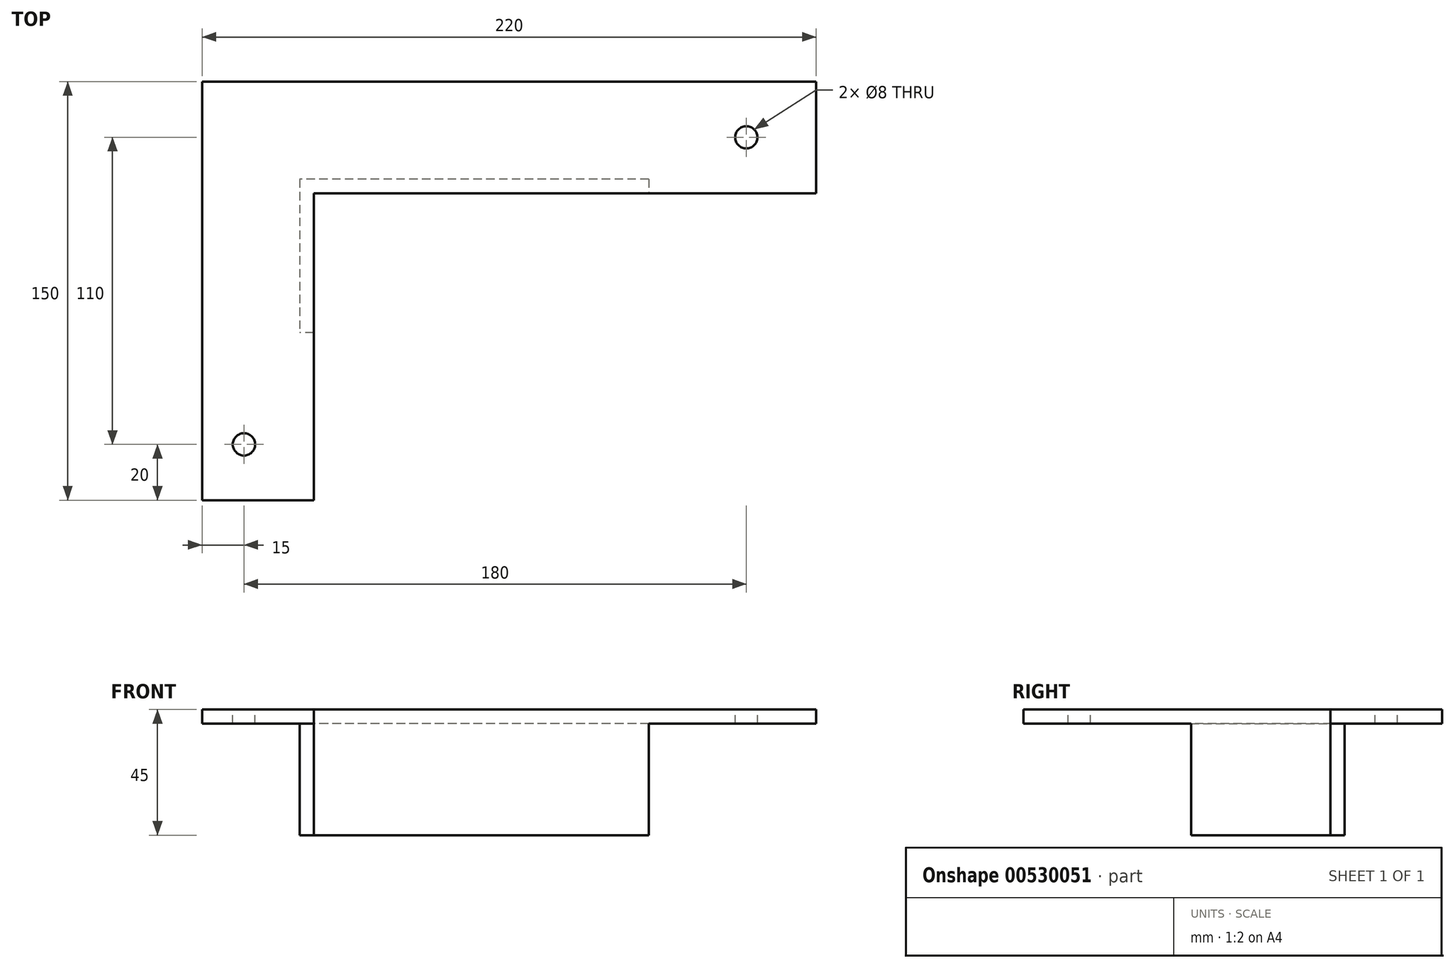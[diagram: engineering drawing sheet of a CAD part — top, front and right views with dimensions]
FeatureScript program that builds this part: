
annotation { "Feature Type Name" : "Feature", "Feature Type Description" : "" }
export const myFeature = defineFeature(function(context is Context, id is Id, definition is map)
    precondition{}
    {
        {
            var Q0;
            Q0=qCreatedBy(makeId("Top.planeOp"),FACE);
            var sketch = newSketch(context, id + "F0", { "sketchPlane" : qUnion([Q0])});
            skLineSegment(sketch, "E0.bottom", {"start": v(110, -20) * mm, "end": v(-110, -20) * mm});
            skLineSegment(sketch, "E0.top", {"start": v(110, 20) * mm, "end": v(-110, 20) * mm});
            skLineSegment(sketch, "E0.left", {"start": v(110, -20) * mm, "end": v(110, 20) * mm});
            skLineSegment(sketch, "E0.right", {"start": v(-110, -20) * mm, "end": v(-110, 20) * mm});
            skPoint(sketch, "E0.middle", {"position": v(0, 0) * mm});
            skSolve(sketch);
        }
        {
            var Q0;
            Q0=makeQuery(id+"F0.imprint","IMPRINT",FACE,{"disambiguationData":[TD([[makeQuery(id+"F0.imprint","IMPRINT",EDGE,{"derivedFrom":sQuery(id+"F0.wireOp",EDGE,"E0.bottom")}),-1.0]])]});
            extrude(context, id + "F1", {"entities" : qUnion([Q0]), "depth" : 5 * mm, "offsetDistance" : 25 * mm});
        }
        {
            var Q0;
            Q0=makeQuery(id+"F1.opExtrude","CAP_FACE",FACE,{"disambiguationData":[OSD([sQuery(id+"F0.wireOp",EDGE,"E0.bottom"),sQuery(id+"F0.wireOp",EDGE,"E0.top"),sQuery(id+"F0.wireOp",EDGE,"E0.left"),sQuery(id+"F0.wireOp",EDGE,"E0.right")])],"isStart":true});
            var sketch = newSketch(context, id + "F2", { "sketchPlane" : qUnion([Q0])});
            skLineSegment(sketch, "E1", {"start": v(110, 20) * mm, "end": v(50, 20) * mm});
            skLineSegment(sketch, "E2", {"start": v(50, 15) * mm, "end": v(50, 20) * mm});
            skLineSegment(sketch, "E3", {"start": v(50, 15) * mm, "end": v(-70, 15) * mm});
            skLineSegment(sketch, "E4", {"start": v(-70, 15) * mm, "end": v(-70, 20) * mm});
            skSolve(sketch);
        }
        {
            var Q0;
            Q0=qSketchRegion(id+"F2",true);
            var Q1;
            {var subQ0=sQuery(id+"F2.wireOp",EDGE,"E2");Q1=makeQuery(id+"F2.imprint","IMPRINT",FACE,{"disambiguationData":[TD([[makeQuery(id+"F2.imprint","IMPRINT",EDGE,{"derivedFrom":subQ0}),1.0]])]});}
            extrude(context, id + "F3", {"entities" : qUnion([Q0, Q1]), "operationType" : NewBodyOperationType.ADD, "depth" : 40 * mm, "offsetDistance" : 25 * mm});
        }
        {
            var Q0;
            Q0=makeQuery(id+"F1.opExtrude","CAP_FACE",FACE,{"disambiguationData":[OSD([sQuery(id+"F0.wireOp",EDGE,"E0.bottom"),sQuery(id+"F0.wireOp",EDGE,"E0.top"),sQuery(id+"F0.wireOp",EDGE,"E0.left"),sQuery(id+"F0.wireOp",EDGE,"E0.right")])],"isStart":true});
            var sketch = newSketch(context, id + "F4", { "sketchPlane" : qUnion([Q0])});
            skLineSegment(sketch, "E5", {"start": v(-110, 20) * mm, "end": v(-110, 130) * mm});
            skLineSegment(sketch, "E6", {"start": v(-110, 130) * mm, "end": v(-70, 130) * mm});
            skLineSegment(sketch, "E7", {"start": v(-70, 130) * mm, "end": v(-70, 20) * mm});
            skSolve(sketch);
        }
        {
            var Q0;
            Q0=qSketchRegion(id+"F4",true);
            var Q1;
            Q1=makeQuery(id+"F4.imprint","IMPRINT",FACE,{"disambiguationData":[TD([[makeQuery(id+"F4.imprint","IMPRINT",EDGE,{"derivedFrom":sQuery(id+"F4.wireOp",EDGE,"E5")}),-1.0]])]});
            extrude(context, id + "F5", {"entities" : qUnion([Q0, Q1]), "operationType" : NewBodyOperationType.ADD, "oppositeDirection" : true, "depth" : 5 * mm, "offsetDistance" : 25 * mm});
        }
        {
            var Q0;
            {var subQ0=sQuery(id+"F0.wireOp",EDGE,"E0.bottom");Q0=makeQuery(id+"F5.boolean.opBoolean","MERGE",FACE,{"derivedFrom":[makeQuery(id+"F1.opExtrude","CAP_FACE",FACE,{"disambiguationData":[OSD([subQ0,sQuery(id+"F0.wireOp",EDGE,"E0.top"),sQuery(id+"F0.wireOp",EDGE,"E0.left"),sQuery(id+"F0.wireOp",EDGE,"E0.right")])],"isStart":true}),makeQuery(id+"F5.opExtrude","CAP_FACE",FACE,{"disambiguationData":[OSD([subQ0,sQuery(id+"F4.wireOp",EDGE,"E5"),sQuery(id+"F4.wireOp",EDGE,"E6"),sQuery(id+"F4.wireOp",EDGE,"E7")])],"isStart":true})]});}
            var sketch = newSketch(context, id + "F6", { "sketchPlane" : qUnion([Q0])});
            skLineSegment(sketch, "E8", {"start": v(-70, 15) * mm, "end": v(-75, 15) * mm});
            skLineSegment(sketch, "E9", {"start": v(-70, 15) * mm, "end": v(-70, 70) * mm});
            skLineSegment(sketch, "E10", {"start": v(-70, 70) * mm, "end": v(-75, 70) * mm});
            skLineSegment(sketch, "E11", {"start": v(-75, 15) * mm, "end": v(-75, 70) * mm});
            skSolve(sketch);
        }
        {
            var Q0;
            Q0=qSketchRegion(id+"F6",true);
            var Q1;
            Q1=makeQuery(id+"F6.imprint","IMPRINT",FACE,{"disambiguationData":[TD([[makeQuery(id+"F6.imprint","IMPRINT",EDGE,{"derivedFrom":sQuery(id+"F6.wireOp",EDGE,"E8")}),-1.0]])]});
            extrude(context, id + "F7", {"entities" : qUnion([Q0, Q1]), "operationType" : NewBodyOperationType.ADD, "depth" : 40 * mm, "offsetDistance" : 25 * mm});
        }
        {
            var Q0;
            {var subQ0=sQuery(id+"F0.wireOp",EDGE,"E0.bottom");Q0=makeQuery(id+"F5.boolean.opBoolean","MERGE",FACE,{"derivedFrom":[makeQuery(id+"F1.opExtrude","CAP_FACE",FACE,{"disambiguationData":[OSD([subQ0,sQuery(id+"F0.wireOp",EDGE,"E0.top"),sQuery(id+"F0.wireOp",EDGE,"E0.left"),sQuery(id+"F0.wireOp",EDGE,"E0.right")])],"isStart":false}),makeQuery(id+"F5.opExtrude","CAP_FACE",FACE,{"disambiguationData":[OSD([subQ0,sQuery(id+"F4.wireOp",EDGE,"E5"),sQuery(id+"F4.wireOp",EDGE,"E6"),sQuery(id+"F4.wireOp",EDGE,"E7")])],"isStart":false})]});}
            var sketch = newSketch(context, id + "F8", { "sketchPlane" : qUnion([Q0])});
            skCircle(sketch, "E12", {"center": v(-95, -110) * mm, "radius": 4 * mm});
            skCircle(sketch, "E13", {"center": v(85, 0) * mm, "radius": 4 * mm});
            skSolve(sketch);
        }
        {
            var Q0;
            Q0=makeQuery(id+"F8.imprint","IMPRINT",FACE,{"disambiguationData":[TD([[makeQuery(id+"F8.imprint","IMPRINT",EDGE,{"derivedFrom":sQuery(id+"F8.wireOp",EDGE,"E12")}),1.0]])]});
            var Q1;
            Q1=makeQuery(id+"F8.imprint","IMPRINT",FACE,{"disambiguationData":[TD([[makeQuery(id+"F8.imprint","IMPRINT",EDGE,{"derivedFrom":sQuery(id+"F8.wireOp",EDGE,"E13")}),1.0]])]});
            var Q2;
            Q2=sQuery(id+"F8.wireOp",EDGE,"E12");
            var Q3;
            Q3=sQuery(id+"F8.wireOp",EDGE,"E13");
            extrude(context, id + "F9", {"entities" : qUnion([Q0, Q1]), "operationType" : NewBodyOperationType.REMOVE, "surfaceEntities" : qUnion([Q2, Q3]), "oppositeDirection" : true, "depth" : 25 * mm, "offsetDistance" : 25 * mm});
        }
    });
